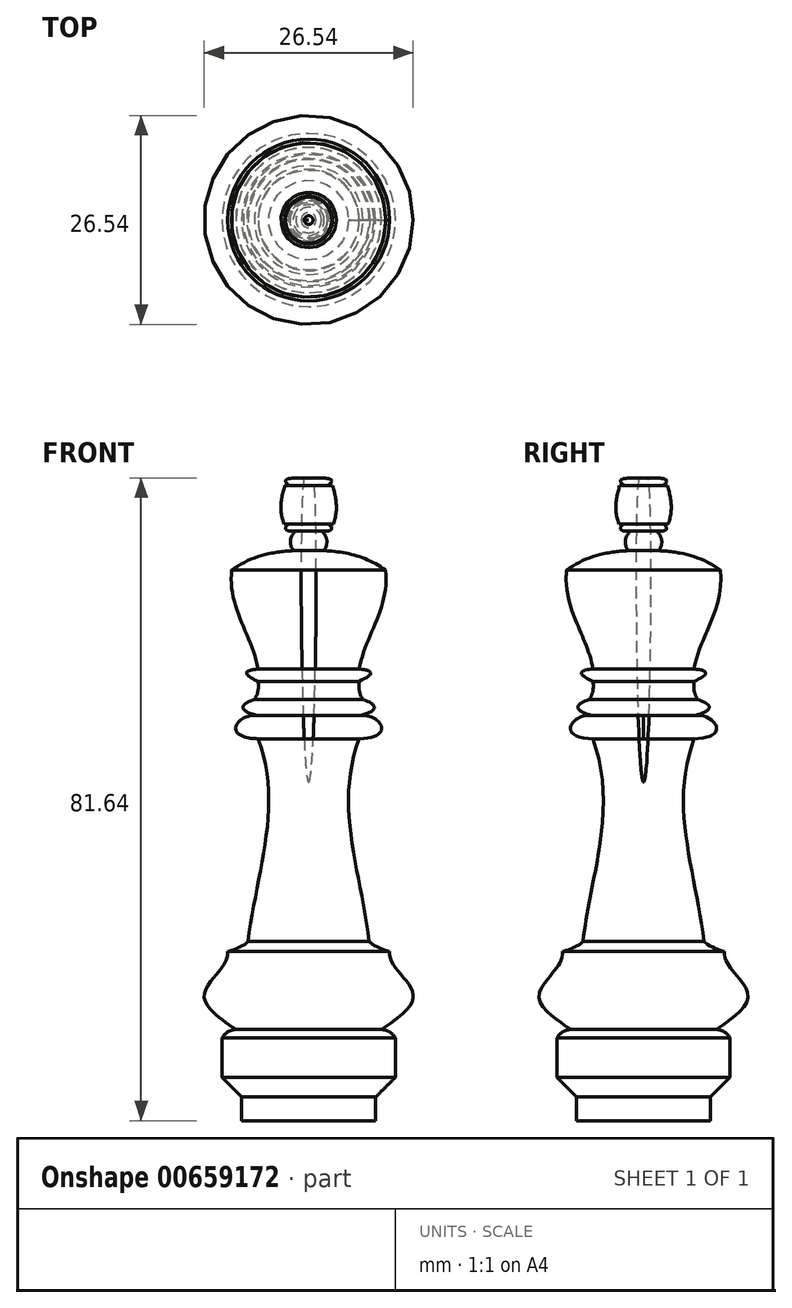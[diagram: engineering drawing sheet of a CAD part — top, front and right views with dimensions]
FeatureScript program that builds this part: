
annotation { "Feature Type Name" : "Feature", "Feature Type Description" : "" }
export const myFeature = defineFeature(function(context is Context, id is Id, definition is map)
    precondition{}
    {
        {
            var Q0;
            Q0=qCreatedBy(makeId("Front.planeOp"),FACE);
            var sketch = newSketch(context, id + "F0", { "sketchPlane" : qUnion([Q0])});
            skLineSegment(sketch, "E0", {"start": v(0, 0) * mm, "end": v(-11, 0) * mm});
            skLineSegment(sketch, "E1", {"start": v(-11, 0) * mm, "end": v(-11, 7.5) * mm});
            skFitSpline(sketch, "E2", {"points": [v(-11, 7.5) * mm, v(-9.23, 8.58) * mm], "startDerivative": vector(1.27, 2.27) * mm, "endDerivative": vector(1.84, 0) * mm});
            skFitSpline(sketch, "E3", {"points": [v(-9.23, 8.58) * mm, v(-13.26, 12.56) * mm, v(-11.59, 15.72) * mm, v(-10.27, 18.47) * mm], "startDerivative": vector(-13.14, 8.87) * mm, "endDerivative": vector(-0.67, 10.22) * mm});
            skFitSpline(sketch, "E4", {"points": [v(-10.27, 18.47) * mm, v(-7.7, 19.79) * mm], "startDerivative": vector(1.49, 0.35) * mm, "endDerivative": vector(1.05, 1.67) * mm});
            skFitSpline(sketch, "E5", {"points": [v(-7.7, 19.79) * mm, v(-6.43, 45.51) * mm], "startDerivative": vector(3.25, 26.6) * mm, "endDerivative": vector(-9.7, 25.56) * mm});
            skFitSpline(sketch, "E6", {"points": [v(-6.43, 45.51) * mm, v(-6.43, 48.46) * mm], "startDerivative": vector(-14.8, 0.35) * mm, "endDerivative": vector(7.5, -1.24) * mm});
            skFitSpline(sketch, "E7", {"points": [v(-6.43, 48.46) * mm, v(-6.9, 50.5) * mm], "startDerivative": vector(-4.71, 0.95) * mm, "endDerivative": vector(8.03, 2.62) * mm});
            skFitSpline(sketch, "E8", {"points": [v(-6.9, 50.5) * mm, v(-6.43, 52.82) * mm], "startDerivative": vector(1.7, 2.38) * mm, "endDerivative": vector(-0.24, 2.12) * mm});
            skFitSpline(sketch, "E9", {"points": [v(-6.43, 52.82) * mm, v(-6.43, 54.36) * mm], "startDerivative": vector(-7.55, 3.3) * mm, "endDerivative": vector(3.75, 0.17) * mm});
            skFitSpline(sketch, "E10", {"points": [v(-6.43, 54.36) * mm, v(-9.78, 66.94) * mm], "startDerivative": vector(-2.1, 12.84) * mm, "endDerivative": vector(1.49, 15) * mm});
            skFitSpline(sketch, "E11", {"points": [v(-9.78, 66.94) * mm, v(-1.96, 69.4) * mm], "startDerivative": vector(7.3, 5.31) * mm, "endDerivative": vector(7.89, 0.33) * mm});
            skFitSpline(sketch, "E12", {"points": [v(-1.96, 69.4) * mm, v(-1.63, 71.92) * mm], "startDerivative": vector(-1.55, 2.48) * mm, "endDerivative": vector(2.5, 2.06) * mm});
            skFitSpline(sketch, "E13", {"points": [v(-1.63, 71.92) * mm, v(-2.6, 72.77) * mm], "startDerivative": vector(-3.51, -0.52) * mm, "endDerivative": vector(2.2, 1.83) * mm});
            skFitSpline(sketch, "E14", {"points": [v(-2.6, 72.77) * mm, v(-3.13, 72.8) * mm], "startDerivative": vector(-0.53, 0) * mm, "endDerivative": vector(-0.54, 0.06) * mm});
            skFitSpline(sketch, "E15", {"points": [v(-3.13, 72.8) * mm, v(-3.04, 77.67) * mm], "startDerivative": vector(-2.05, 5.19) * mm, "endDerivative": vector(1.34, 4.67) * mm});
            skFitSpline(sketch, "E16", {"points": [v(-3.04, 77.67) * mm, v(-2.44, 77.67) * mm], "startDerivative": vector(0.6, 0) * mm, "endDerivative": vector(0.6, 0) * mm});
            skFitSpline(sketch, "E17", {"points": [v(-2.44, 77.67) * mm, v(-0.5, 78.63) * mm], "startDerivative": vector(-4.62, 3.3) * mm, "endDerivative": vector(3.25, -0.04) * mm});
            skFitSpline(sketch, "E18", {"points": [v(-0.5, 78.63) * mm, v(0, 40) * mm], "startDerivative": vector(-2.42, 2.15) * mm, "endDerivative": vector(2.87, 0.1) * mm});
            skLineSegment(sketch, "E19", {"start": v(0, 40) * mm, "end": v(0, 0) * mm});
            skSolve(sketch);
        }
        {
            var Q0;
            Q0=makeQuery(id+"F0.imprint","IMPRINT",FACE,{"disambiguationData":[TD([[makeQuery(id+"F0.imprint","IMPRINT",EDGE,{"derivedFrom":sQuery(id+"F0.wireOp",EDGE,"E0")}),-1.0]])]});
            var Q1;
            Q1=sQuery(id+"F0.wireOp",EDGE,"E19");
            revolve(context, id + "F1", {"surfaceOperationType" : NewSurfaceOperationType.NEW, "entities" : qUnion([Q0]), "axis" : qUnion([Q1]), "revolveType" : RevolveType.FULL});
        }
        {
            var Q0;
            Q0=makeQuery(id+"F1.opRevolve","SWEPT_EDGE",EDGE,{"disambiguationData":[OSD([sQuery(id+"F0.wireOp",EDGE,"E0"),sQuery(id+"F0.wireOp",EDGE,"E1")])]});
            chamfer(context, id + "F2", {"entities" : qUnion([Q0]), "width" : 2.5 * mm, "tangentPropagation" : true});
        }
        {
            var Q0;
            Q0=makeQuery(id+"F1.opRevolve","SWEPT_FACE",FACE,{"disambiguationData":[OSD([sQuery(id+"F0.wireOp",EDGE,"E0")])]});
            extrude(context, id + "F3", {"entities" : qUnion([Q0]), "operationType" : NewBodyOperationType.ADD, "depth" : 3 * mm, "offsetDistance" : 25 * mm});
        }
    });
